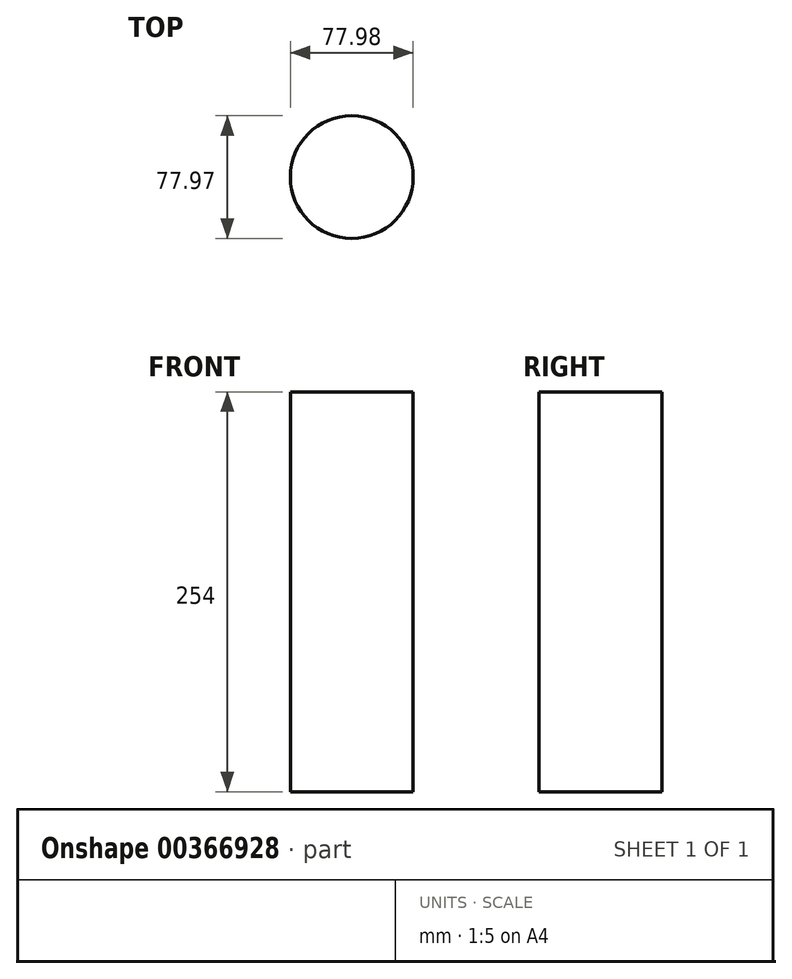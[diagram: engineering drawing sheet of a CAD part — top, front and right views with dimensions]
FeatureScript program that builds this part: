
annotation { "Feature Type Name" : "Feature", "Feature Type Description" : "" }
export const myFeature = defineFeature(function(context is Context, id is Id, definition is map)
    precondition{}
    {
        {
            var Q0;
            Q0=qCreatedBy(makeId("Top.planeOp"),FACE);
            var sketch = newSketch(context, id + "F0", { "sketchPlane" : qUnion([Q0])});
            skArc(sketch, "E0", {"start": v(0, -39.17) * mm, "mid": v(39.18, -0.18) * mm, "end": v(0, 38.8) * mm});
            skArc(sketch, "E1", {"start": v(0, 38.8) * mm, "mid": v(-38.8, -0.18) * mm, "end": v(0, -39.17) * mm});
            skSolve(sketch);
        }
        {
            var Q0;
            Q0 = qSketchRegion(id + "F0", true);
            extrude(context, id + "F1", {"entities" : qUnion([Q0]), "depth" : 254 * mm});
        }
    });
